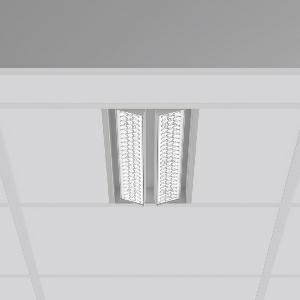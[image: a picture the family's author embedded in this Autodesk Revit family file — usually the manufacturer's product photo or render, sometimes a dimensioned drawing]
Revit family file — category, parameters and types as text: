
# Revit family: tx-move_901736_004_3_76_224b
name_source: partatom
category: Lighting Fixtures
units: mm (PartAtom-declared; Revit-internal decimal feet)

## family parameters
Cut with Voids When Loaded = No
Host = Face
Light Source = No
Part Type = Normal
Room Calculation Point = No
Round Connector Dimension = Use Diameter
Shared = No

## types (1)
- MultiLumen 1 (1 x LED Modul 835, 2775 lm, 3500)
    Apparent Load = 35 VA
    CIE Flux Codes = 88 96 99 100 100
    Color Rendering = 80
    Color Temperature = 3500
    Default Elevation = 1800 mm
    Description = Series: TX-MOVE
Einlege/Einbau-Flächenstrahler. Housing: sheet steel, powder-coated. 2xSwivel range: 90°. High-efficiency LED units with optimum light control thanks to clear plastic (PC) lens optics. Spezielle Mikrostrukturen reduzieren Gelbsaum. Symmetrical light distribution. Suitable for laying in grid ceiling module 625. Connected converter included in separate gearbox.Suitable for through-wiring.MultiLumen: Luminous flux adjustable in 3 steps. Accessories: Mounting frame for installation in suspended ceilings. Environmentally friendly and resource-saving due to replaceable and recyclable components. 
Colour: silver, matt (approx. RAL 9006)
Length: 622 mm
Width: 190 mm
Height: 39 mm
Cut-out length: 602 mm
Cut-out width: 174 mm
Recess height: 100 mm
Lamp: LED
Socket: without socket
Colour temperature: 3500K
Colour rendering index (CRI): 80
System power: 35 W
Rated luminous flux: 5550 lm
Luminous efficiency: 159 lm/W
System power 2: 47 W
Rated luminous flux 2: 7200 lm
Luminous efficiency 2: 153 lm/W
System power 3: 68 W
Rated luminous flux 3: 9900 lm
Luminous efficiency 3: 146 lm/W
Control gear: Dimmable EVG, DALI
Protection class: I
Type of protection: IP 20
    Height = 0 mm  [stored 0 ft]
    Lamp = 1 x LED Modul 835
    Lamp Light Flux = 2775 lm
    Lamp count = 1
    Length = 622 mm
    Lifetime = 50000 h
    Luminous efficacy = 159 lm/W
    Manufacturer = RZB
    ModVariant = No
    Model = 901736.004.3.76
    Mounting Place = Ceiling, Wall
    Mounting Type = Recessed
    Number of Poles = 1
    OnlyDefault = Yes
    Power Factor = 1
    Product Name = TX-MOVE
    Product group = Recessed projectors
    ProductGroupID = 401
    Protection Class = Protection class I
    Protection Degree = IP 20
    RLX_Detail_Level = 1
    RLX_Emergency_Light_Flux = 0 lm
    RLX_Emergency_Type = 0
    RLX_Emergency_Type_DB = No
    RlxData = <blob elided: 34453 chars, md5=080d6ee9>
    Socket = socket
    Standby Power = 0 W
    System Light Flux = 5550 lm
    System Power = 35 W
    Type Comments = MultiLumen 1
    Type Image = 901737.004.jpg
    URL = http://relux.com
    VarID = multilumen_1
    Voltage = 230 V
    Voltage Range = 220-240 V
    Weight = 0.00 kg
    Width = 190 mm  [stored 0.62336 ft]

note: [stored X ft] marks values corroborated as IEEE doubles in the binary element streams (Revit-internal decimal feet)

## geometry (parser evidence)
native form markers: Blend x4, Sweep x14
no freeform markers — native parametric forms only
